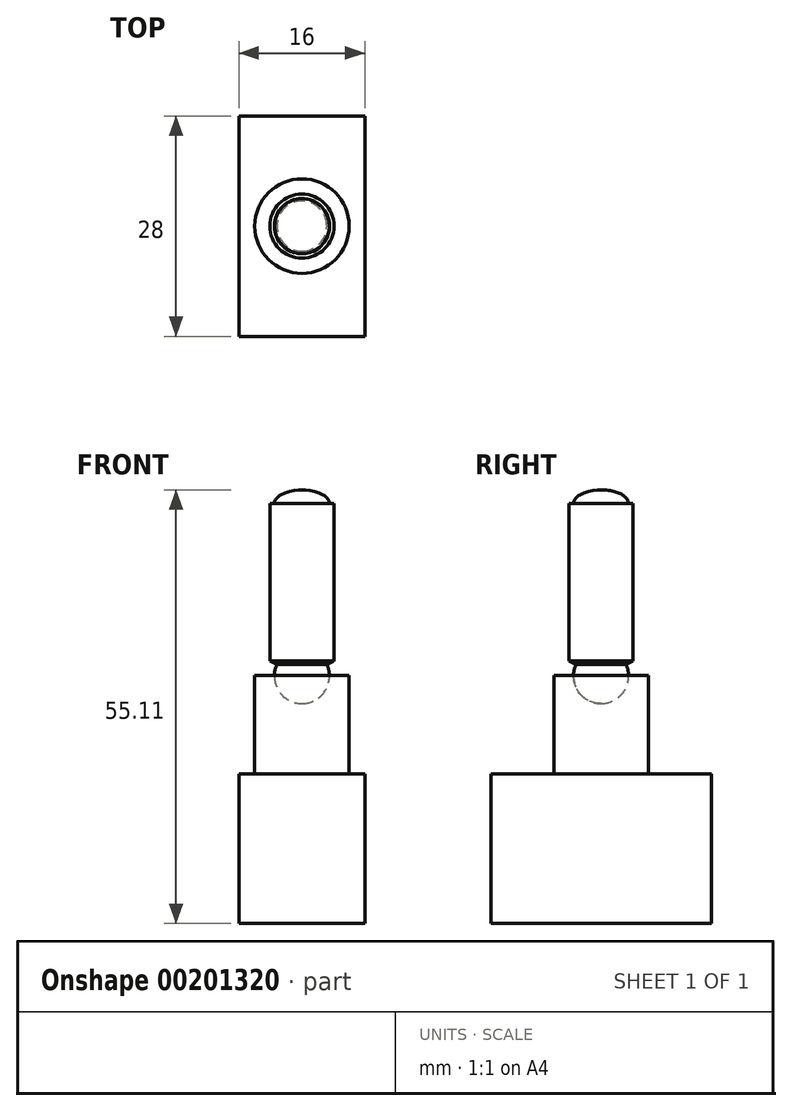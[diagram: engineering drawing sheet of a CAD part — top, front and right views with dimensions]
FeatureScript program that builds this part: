
annotation { "Feature Type Name" : "Feature", "Feature Type Description" : "" }
export const myFeature = defineFeature(function(context is Context, id is Id, definition is map)
    precondition{}
    {
        {
            var Q0;
            Q0=qCreatedBy(makeId("Top.planeOp"),FACE);
            var sketch = newSketch(context, id + "F0", { "sketchPlane" : qUnion([Q0])});
            skCircle(sketch, "E0", {"center": v(0, 0) * mm, "radius": 6 * mm});
            skSolve(sketch);
        }
        {
            var Q0;
            Q0=makeQuery(id+"F0.imprint","IMPRINT",FACE,{"disambiguationData":[TD([[makeQuery(id+"F0.imprint","IMPRINT",EDGE,{"derivedFrom":sQuery(id+"F0.wireOp",EDGE,"E0")}),1.0]])]});
            extrude(context, id + "F1", {"entities" : qUnion([Q0]), "depth" : 12.5 * mm});
        }
        {
            var Q0;
            Q0=qCreatedBy(makeId("Right.planeOp"),FACE);
            var sketch = newSketch(context, id + "F2", { "sketchPlane" : qUnion([Q0])});
            skLineSegment(sketch, "E1.bottom", {"start": v(14, 0) * mm, "end": v(-14, 0) * mm});
            skLineSegment(sketch, "E1.top", {"start": v(14, -19) * mm, "end": v(-14, -19) * mm});
            skLineSegment(sketch, "E1.left", {"start": v(14, 0) * mm, "end": v(14, -19) * mm});
            skLineSegment(sketch, "E1.right", {"start": v(-14, 0) * mm, "end": v(-14, -19) * mm});
            skPoint(sketch, "E1.middle", {"position": v(0, -9.5) * mm});
            skCircle(sketch, "E2", {"center": v(0, 12.45) * mm, "radius": 3.5 * mm});
            skLineSegment(sketch, "E3", {"start": v(0, 15.95) * mm, "end": v(0, 8.95) * mm});
            skLineSegment(sketch, "E4", {"start": v(0, 12.45) * mm, "end": v(3.17, 13.93) * mm, "construction": true});
            skLineSegment(sketch, "E5", {"start": v(0, 12.45) * mm, "end": v(3.5, 12.45) * mm});
            skLineSegment(sketch, "E6", {"start": v(3.17, 13.93) * mm, "end": v(4.07, 14.36) * mm});
            skLineSegment(sketch, "E7", {"start": v(4.07, 14.36) * mm, "end": v(4.07, 34.36) * mm});
            skLineSegment(sketch, "E8", {"start": v(4.07, 34.36) * mm, "end": v(0, 34.36) * mm});
            skLineSegment(sketch, "E9", {"start": v(0, 34.36) * mm, "end": v(0, 15.95) * mm});
            skEllipse(sketch, "E10", {"center": v(0, 34.36) * mm, "majorRadius": 3.5 * mm, "minorRadius": 1.75 * mm, "majorAxis": v(1, 0)});
            skLineSegment(sketch, "E11", {"start": v(0, 34.36) * mm, "end": v(0, 36.1) * mm});
            skSolve(sketch);
        }
        {
            var Q0;
            Q0=makeQuery(id+"F2.imprint","IMPRINT",FACE,{"disambiguationData":[TD([[makeQuery(id+"F2.imprint","IMPRINT",EDGE,{"derivedFrom":sQuery(id+"F2.wireOp",EDGE,"E1.bottom")}),1.0]])]});
            extrude(context, id + "F3", {"entities" : qUnion([Q0]), "endBound" : BoundingType.SYMMETRIC, "depth" : 16 * mm});
        }
        {
            var Q0;
            {var subQ0=sQuery(id+"F2.wireOp",EDGE,"E6");Q0=makeQuery(id+"F2.imprint","IMPRINT",FACE,{"disambiguationData":[TD([[makeQuery(id+"F2.imprint","IMPRINT",EDGE,{"derivedFrom":subQ0}),1.0]])]});}
            var Q1;
            {var subQ0=sQuery(id+"F2.wireOp",EDGE,"E5");Q1=makeQuery(id+"F2.imprint","IMPRINT",FACE,{"disambiguationData":[TD([[makeQuery(id+"F2.imprint","IMPRINT",EDGE,{"derivedFrom":subQ0}),1.0]])]});}
            var Q2;
            {var subQ1=sQuery(id+"F2.wireOp",EDGE,"E8");var subQ3=sQuery(id+"F2.wireOp",EDGE,"E10");var subQ4=makeQuery(id+"F2.imprint","INTERSECT",VERTEX,{"derivedFrom":[subQ1,subQ3]});Q2=makeQuery(id+"F2.imprint","IMPRINT",FACE,{"disambiguationData":[TD([[makeQuery(id+"F2.imprint","IMPRINT",EDGE,{"disambiguationData":[TD([[subQ4,1.0]])],"derivedFrom":subQ3}),1.0]])]});}
            var Q3;
            {var subQ0=sQuery(id+"F2.wireOp",EDGE,"E11");Q3=makeQuery(id+"F2.imprint","IMPRINT",FACE,{"disambiguationData":[TD([[makeQuery(id+"F2.imprint","IMPRINT",EDGE,{"derivedFrom":subQ0}),-1.0]])]});}
            var Q4;
            {var subQ3=sQuery(id+"F2.wireOp",EDGE,"E5");Q4=makeQuery(id+"F2.imprint","IMPRINT",FACE,{"disambiguationData":[TD([[makeQuery(id+"F2.imprint","IMPRINT",EDGE,{"derivedFrom":subQ3}),-1.0]])]});}
            var Q5;
            Q5=sQuery(id+"F2.wireOp",EDGE,"E9");
            revolve(context, id + "F4", {"entities" : qUnion([Q0, Q1, Q2, Q3, Q4]), "axis" : qUnion([Q5]), "revolveType" : RevolveType.FULL});
        }
    });
